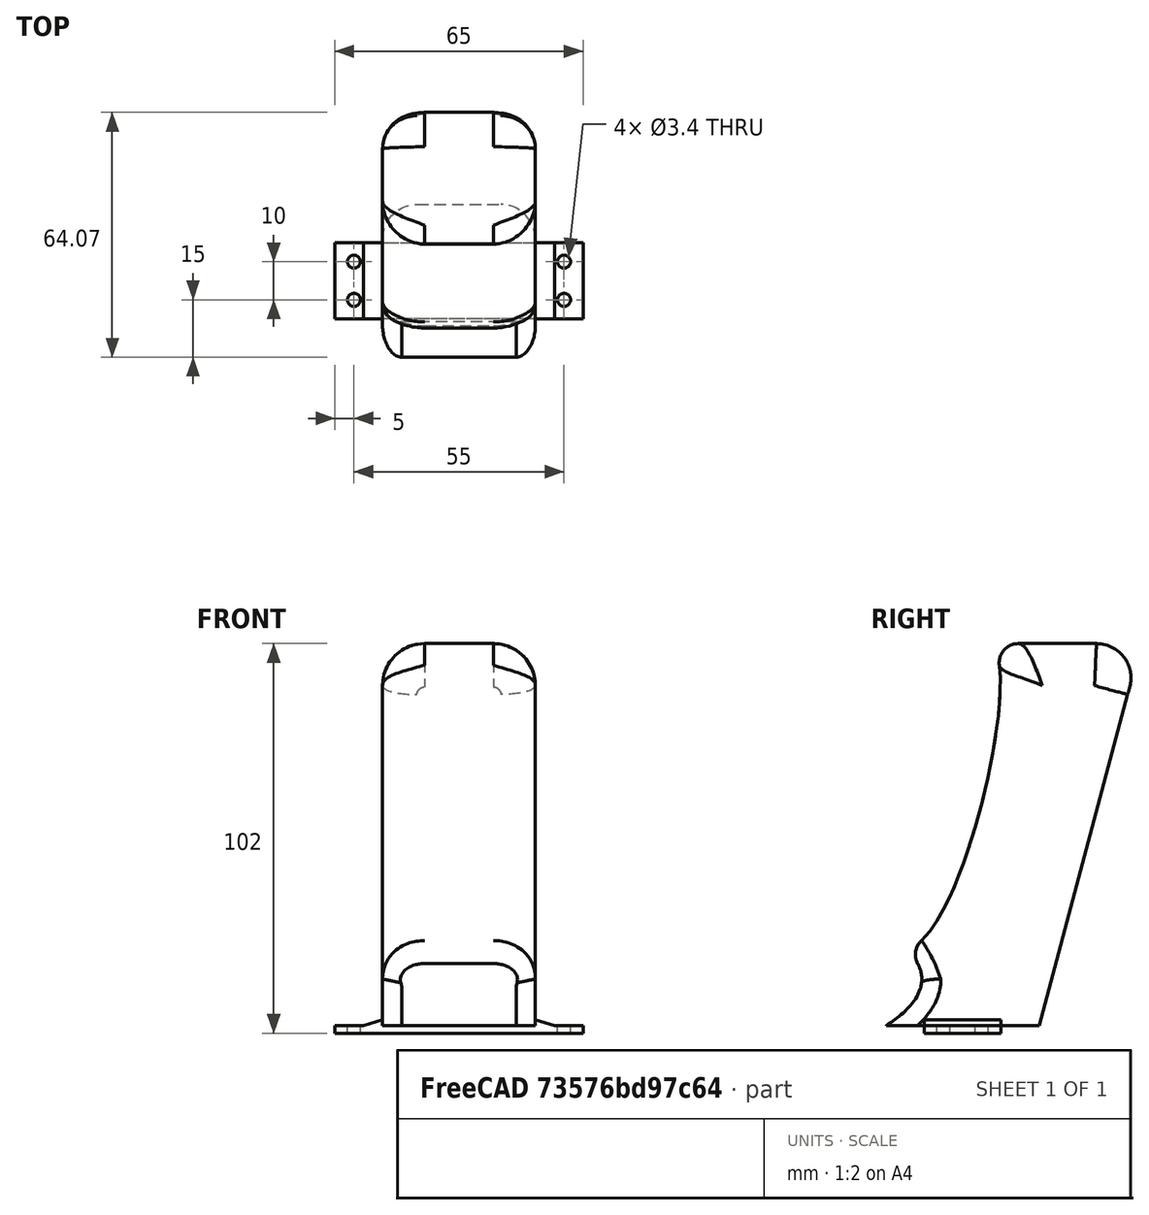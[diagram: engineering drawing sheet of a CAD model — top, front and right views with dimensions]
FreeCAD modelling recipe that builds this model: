
FCSTD DOCUMENT  (FreeCAD 0.21R33668 +26 (Git))
Label: Handgrip
License: All rights reserved
LicenseURL: https://en.wikipedia.org/wiki/All_rights_reserved
objects: Sketcher::SketchObject×4, PartDesign::Fillet×4, App::DocumentObjectGroup×3, PartDesign::Pad×2, PartDesign::CoordinateSystem×2, Spreadsheet::Sheet×1, PartDesign::Hole×1, PartDesign::Pocket×1, App::FeaturePython×1, PartDesign::Chamfer×1, PartDesign::Body×1, App::Part×1, Mesh::Feature×1
note: 25 computed .brp shape members not serialized (recipe doc carries the construction recipe); baked Part::Feature solids carry a one-line shape summary decoded from their .brp
EXTERNAL_REF file=Casing2.FCStd obj=Spreadsheet

FEATURE [Spreadsheet::Sheet] Spreadsheet
  cells = B2='interface_width; C2(interface_width)==<<Casing2>>#Spreadsheet.interface_width; E2='handgrip_width; F2(handgrip_width)==40 mm; B3='interface_height; C3(interface_height)==<<Casing2>>#Spreadsheet.beams_width * 2; E3='handgrip_depth; F3(handgrip_depth)==40 mm; B4='interface_thickness; C4(interface_thickness)==<<Casing2>>#Spreadsheet.walls_thickness; E4='handgrip_length; F4(handgrip_length)==100 mm; B5='screw_radius; C5(screw_radius)==<<Casing2>>#Spreadsheet.screw_radius; B6='slant; C6(slant)==<<Casing2>>#Spreadsheet.slant
FEATURE [Sketcher::SketchObject] Sketch
  FullyConstrained = true
  MapMode = 5
  Support = -> [XY_Plane]
  expr: Constraints[10] = Spreadsheet.interface_height
  expr: Constraints[9] = Spreadsheet.interface_width
  sketch-geometry (4):
    g0: LineSegment StartX=-32.5 StartY=10 StartZ=0 EndX=32.5 EndY=10 EndZ=0
    g1: LineSegment StartX=32.5 StartY=10 StartZ=0 EndX=32.5 EndY=-10 EndZ=0
    g2: LineSegment StartX=32.5 StartY=-10 StartZ=0 EndX=-32.5 EndY=-10 EndZ=0
    g3: LineSegment StartX=-32.5 StartY=-10 StartZ=0 EndX=-32.5 EndY=10 EndZ=0
  constraints (11):
    c: Coincident(g0,g1)
    c: Coincident(g1,g2)
    c: Coincident(g2,g3)
    c: Coincident(g3,g0)
    c: Horizontal(g0)
    c: Horizontal(g2)
    c: Vertical(g1)
    c: Vertical(g3)
    c: Symmetric(g2,g0,g-1)
    c: DistanceX(g0,g0) = 65
    c: DistanceY(g3,g3) = 20
FEATURE [PartDesign::Pad] Pad
  Direction = (0,0,1)
  Length = 2
  Length2 = 10
  Profile = -> Sketch
  ReferenceAxis = -> Sketch [N_Axis]
  Type = 0
  expr: Length = Spreadsheet.interface_thickness
FEATURE [Sketcher::SketchObject] Sketch001
  FullyConstrained = true
  MapMode = 5
  Placement = pos=(0,0,0) rot=(1,0,0;3.14159rad)
  Support = -> [Pad]
  expr: Constraints[0] = Spreadsheet.screw_radius
  expr: Constraints[13] = Spreadsheet.interface_width
  expr: Constraints[14] = Spreadsheet.interface_height
  expr: Constraints[15] = Spreadsheet.interface_height / 4
  expr: Constraints[16] = Spreadsheet.interface_height / 4
  expr: Constraints[17] = Spreadsheet.interface_height / 4
  expr: Constraints[18] = Spreadsheet.interface_height / 4
  expr: Constraints[19] = Spreadsheet.interface_height / 4
  expr: Constraints[1] = Spreadsheet.screw_radius
  expr: Constraints[20] = Spreadsheet.interface_height / 4
  expr: Constraints[21] = Spreadsheet.interface_height / 4
  expr: Constraints[22] = Spreadsheet.interface_height / 4
  expr: Constraints[2] = Spreadsheet.screw_radius
  expr: Constraints[3] = Spreadsheet.screw_radius
  sketch-geometry (8):
    g0: Circle CenterX=-27.5 CenterY=5 CenterZ=0 NormalX=0 NormalY=0 NormalZ=1 AngleXU=0 Radius=1.5
    g1: Circle CenterX=-27.5 CenterY=-5 CenterZ=0 NormalX=0 NormalY=0 NormalZ=1 AngleXU=0 Radius=1.5
    g2: Circle CenterX=27.5 CenterY=5 CenterZ=0 NormalX=0 NormalY=0 NormalZ=1 AngleXU=0 Radius=1.5
    g3: Circle CenterX=27.5 CenterY=-5 CenterZ=0 NormalX=0 NormalY=0 NormalZ=1 AngleXU=0 Radius=1.5
    g4: LineSegment StartX=-32.5 StartY=10 StartZ=0 EndX=32.5 EndY=10 EndZ=0
    g5: LineSegment StartX=32.5 StartY=10 StartZ=0 EndX=32.5 EndY=-10 EndZ=0
    g6: LineSegment StartX=32.5 StartY=-10 StartZ=0 EndX=-32.5 EndY=-10 EndZ=0
    g7: LineSegment StartX=-32.5 StartY=-10 StartZ=0 EndX=-32.5 EndY=10 EndZ=0
  constraints (23):
    c: Radius(g0) = 1.5
    c: Radius(g1) = 1.5
    c: Radius(g2) = 1.5
    c: Radius(g3) = 1.5
    c: Coincident(g4,g5)
    c: Coincident(g5,g6)
    c: Coincident(g6,g7)
    c: Coincident(g7,g4)
    c: Horizontal(g4)
    c: Horizontal(g6)
    c: Vertical(g5)
    c: Vertical(g7)
    c: Symmetric(g4,g6,g-1)
    c: DistanceX(g4,g4) = 65
    c: DistanceY(g7,g7) = 20
    c: DistanceX(g4,g0) = 5
    c: DistanceX(g2,g4) = 5
    c: DistanceX(g3,g5) = 5
    c: DistanceX(g6,g1) = 5
    c: DistanceY(g0,g4) = 5
    c: DistanceY(g6,g1) = 5
    c: DistanceY(g2,g4) = 5
    c: DistanceY(g5,g3) = 5
FEATURE [PartDesign::Hole] Hole
  BaseFeature = -> Pad
  CustomThreadClearance = 0
  Depth = 113.066
  DepthType = 1
  Diameter = 3.4
  DrillForDepth = false
  DrillPoint = 1
  DrillPointAngle = 118
  HoleCutCountersinkAngle = 90
  HoleCutCustomValues = false
  HoleCutDepth = 0
  HoleCutDiameter = 6.1
  HoleCutType = 0
  ModelThread = false
  Profile = -> Sketch001
  Tapered = false
  TaperedAngle = 90
  ThreadClass = 0
  ThreadDepth = 113.066
  ThreadDepthType = 0
  ThreadDirection = 0
  ThreadFit = 0
  ThreadSize = 9
  ThreadType = 1
  Threaded = false
  UseCustomThreadClearance = false
FEATURE [Sketcher::SketchObject] Sketch002
  FullyConstrained = true
  MapMode = 5
  Placement = pos=(0,0,2) rot=(0,0,1;0rad)
  Support = -> [Hole]
  expr: Constraints[10] = Spreadsheet.handgrip_depth
  expr: Constraints[9] = Spreadsheet.handgrip_width
  sketch-geometry (4):
    g0: LineSegment StartX=-20 StartY=20 StartZ=0 EndX=20 EndY=20 EndZ=0
    g1: LineSegment StartX=20 StartY=20 StartZ=0 EndX=20 EndY=-20 EndZ=0
    g2: LineSegment StartX=20 StartY=-20 StartZ=0 EndX=-20 EndY=-20 EndZ=0
    g3: LineSegment StartX=-20 StartY=-20 StartZ=0 EndX=-20 EndY=20 EndZ=0
  constraints (11):
    c: Coincident(g0,g1)
    c: Coincident(g1,g2)
    c: Coincident(g2,g3)
    c: Coincident(g3,g0)
    c: Horizontal(g0)
    c: Horizontal(g2)
    c: Vertical(g1)
    c: Vertical(g3)
    c: Symmetric(g0,g2,g-1)
    c: DistanceX(g0,g0) = 40
    c: DistanceY(g3,g3) = 40
FEATURE [PartDesign::Pad] Pad001
  BaseFeature = -> Hole
  Direction = (0,0.267949,1)
  Length = 100
  Length2 = 10
  Profile = -> Sketch002
  ReferenceAxis = -> Sketch002 [N_Axis]
  Type = 0
  UseCustomVector = true
  expr: .Direction.y = tan(Spreadsheet.slant)
  expr: Length = Spreadsheet.handgrip_length
FEATURE [Sketcher::SketchObject] Sketch003
  ExternalGeometry = -> [Pad001]
  FullyConstrained = true
  MapMode = 5
  Placement = pos=(-20,0,0) rot=(0.57735,-0.57735,-0.57735;2.0944rad)
  Support = -> [Pad001]
  sketch-geometry (14):
    g0: Circle CenterX=20 CenterY=2 CenterZ=0 NormalX=0 NormalY=0 NormalZ=1 AngleXU=0 Radius=1
    g1: Circle CenterX=4.64102 CenterY=12 CenterZ=0 NormalX=0 NormalY=0 NormalZ=1 AngleXU=0 Radius=1
    g2: Circle CenterX=14.641 CenterY=22 CenterZ=0 NormalX=0 NormalY=0 NormalZ=1 AngleXU=0 Radius=1
    g3: BSplineCurve PolesCount=3 KnotsCount=2 Degree=2 IsPeriodic=0
    g4: GeomPoint X=20 Y=2 Z=0
    g5: GeomPoint X=14.641 Y=22 Z=0
    g6-g9: Circle x4 (B-spline internal-alignment scaffolding for g10; pole/knot coordinates omitted)
    g10: BSplineCurve PolesCount=4 KnotsCount=2 Degree=3 IsPeriodic=0
    g11: GeomPoint X=14.641 Y=22 Z=0
    g12: GeomPoint X=-6.79492 Y=102 Z=0
    g13: LineSegment StartX=-6.79492 StartY=102 StartZ=0 EndX=20 EndY=2 EndZ=0
  constraints (28):
    c: Weight(g0) = 1
    c: Equal(g0,g1)
    c: Equal(g0,g2)
    c: InternalAlignment(g0,g3)
    c: InternalAlignment(g1,g3)
    c: InternalAlignment(g2,g3)
    c: InternalAlignment(g4,g3)
    c: InternalAlignment(g5,g3)
    c: Weight(g6) = 1
    c: Coincident(g10,g3)
    c: Equal(g6,g7)
    c: Equal(g6,g8)
    c: Equal(g6,g9)
    c: InternalAlignment(g6-g9 -> g10) x4
    c: InternalAlignment(g11,g10)
    c: InternalAlignment(g12,g10)
    c: DistanceY(g-7,g3) = 20
    c: DistanceX(g1,g3) = 10
    c: DistanceY(g1,g3) = 10
    c: DistanceX(g7,g3) = 15
    c: DistanceY(g3,g7) = 3
    c: DistanceY(g8,g-6) = 3
    c: DistanceX(g8,g-6) = 10
    c: PointOnObject(g3,g-6)
    c: Coincident(g10,g-6)
    c: Coincident(g3,g-7)
    c: Coincident(g13,g10)
    c: Coincident(g13,g3)
FEATURE [PartDesign::Pocket] Pocket
  BaseFeature = -> Pad001
  Direction = (1,0,0)
  Length = 5
  Length2 = 5
  Profile = -> Sketch003
  ReferenceAxis = -> Sketch003 [N_Axis]
  Type = 1
FEATURE [PartDesign::Fillet] Fillet
  Base = -> Pocket [Edge46]
  BaseFeature = -> Pocket
  Radius = 5
  SupportTransform = false
  UseAllEdges = false
FEATURE [PartDesign::Fillet] Fillet001
  Base = -> Fillet [Edge4,Edge17]
  BaseFeature = -> Fillet
  Radius = 11
  SupportTransform = false
  UseAllEdges = false
FEATURE [PartDesign::Fillet] Fillet002
  Base = -> Fillet001 [Edge17,Edge28]
  BaseFeature = -> Fillet001
  Radius = 5
  SupportTransform = false
  UseAllEdges = false
FEATURE [PartDesign::Fillet] Fillet003
  Base = -> Fillet002 [Edge5,Edge23]
  BaseFeature = -> Fillet002
  Radius = 9
  SupportTransform = false
  UseAllEdges = false
FEATURE [App::DocumentObjectGroup] Parts
FEATURE [PartDesign::CoordinateSystem] LCS_Origin
  AttacherType = Attacher::AttachEngine3D
  MapMode = 2
  Support = -> [X_Axis001]
FEATURE [App::DocumentObjectGroup] Constraints
FEATURE [App::FeaturePython] Variables  # WARN: FeaturePython — macro-defined, semantics opaque (R4)
  Type = App::PropertyContainer
FEATURE [App::DocumentObjectGroup] Configurations
FEATURE [PartDesign::CoordinateSystem] LCS_screw
  AttacherType = Attacher::AttachEngine3D
  MapMode = 11
  Placement = pos=(-27.5,-5,0) rot=(0.707107,0.707107,0;3.14159rad)
  Support = -> [Fillet003]
FEATURE [PartDesign::Chamfer] Chamfer
  Angle = 45
  Base = -> Fillet003 [Edge6,Edge53]
  BaseFeature = -> Fillet003
  ChamferType = 1
  FlipDirection = false
  Size = 1.5
  Size2 = 5
  SupportTransform = false
  UseAllEdges = false
FEATURE [PartDesign::Body] Body  label="Körper"
  Group = -> [Sketch,Pad,Sketch001,Hole,Sketch002,Pad001,Sketch003,Pocket,Fillet,Fillet001,Fillet002,Fillet003,Chamfer]
  Origin = -> Origin
  Tip = -> Chamfer
FEATURE [App::Part] Model
  AssemblyType = Part::Link
  Group = -> [LCS_Origin,Constraints,Variables,Configurations,Body,LCS_screw]
  Origin = -> Origin001
  Type = Assembly
FEATURE [Mesh::Feature] Mesh  label="Körper (Meshed)"
